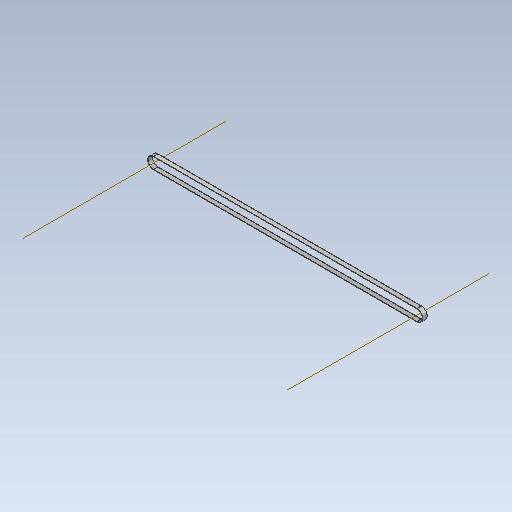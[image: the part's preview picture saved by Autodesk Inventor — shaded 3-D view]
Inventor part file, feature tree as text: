
AUTODESK INVENTOR PART (.ipt)
format: ipt  version: 2020 (Build 240168000, 168)  size: 93,696 bytes
history: native  units: mm (DEFAULTED — no unit token found)
features: other x4, plane x2, sketch x1, sweep x1
ambient origin geometry x8: Origin, YZ Plane, XZ Plane, XY Plane, X Axis, Y Axis, Z Axis, Center Point
bodies: Solid1 (feature_tree)
feature tree (8):
  sketch  "Sketch Path"  dims[d0=6.35mm d2=0.0mm d4=0.254mm d5=0.381mm d6=0.0mm d7=0.0mm d8=0.0mm d9=0.0mm d10=0.0mm d11=0.0mm]
  other  "Cross Section Plane"
  other  "Work Axis1"
  other  "Work Axis2"
  plane  "Work Plane2"
  plane  "Work Plane3"
  sweep  "Belt"
  other  "Cross Section"
